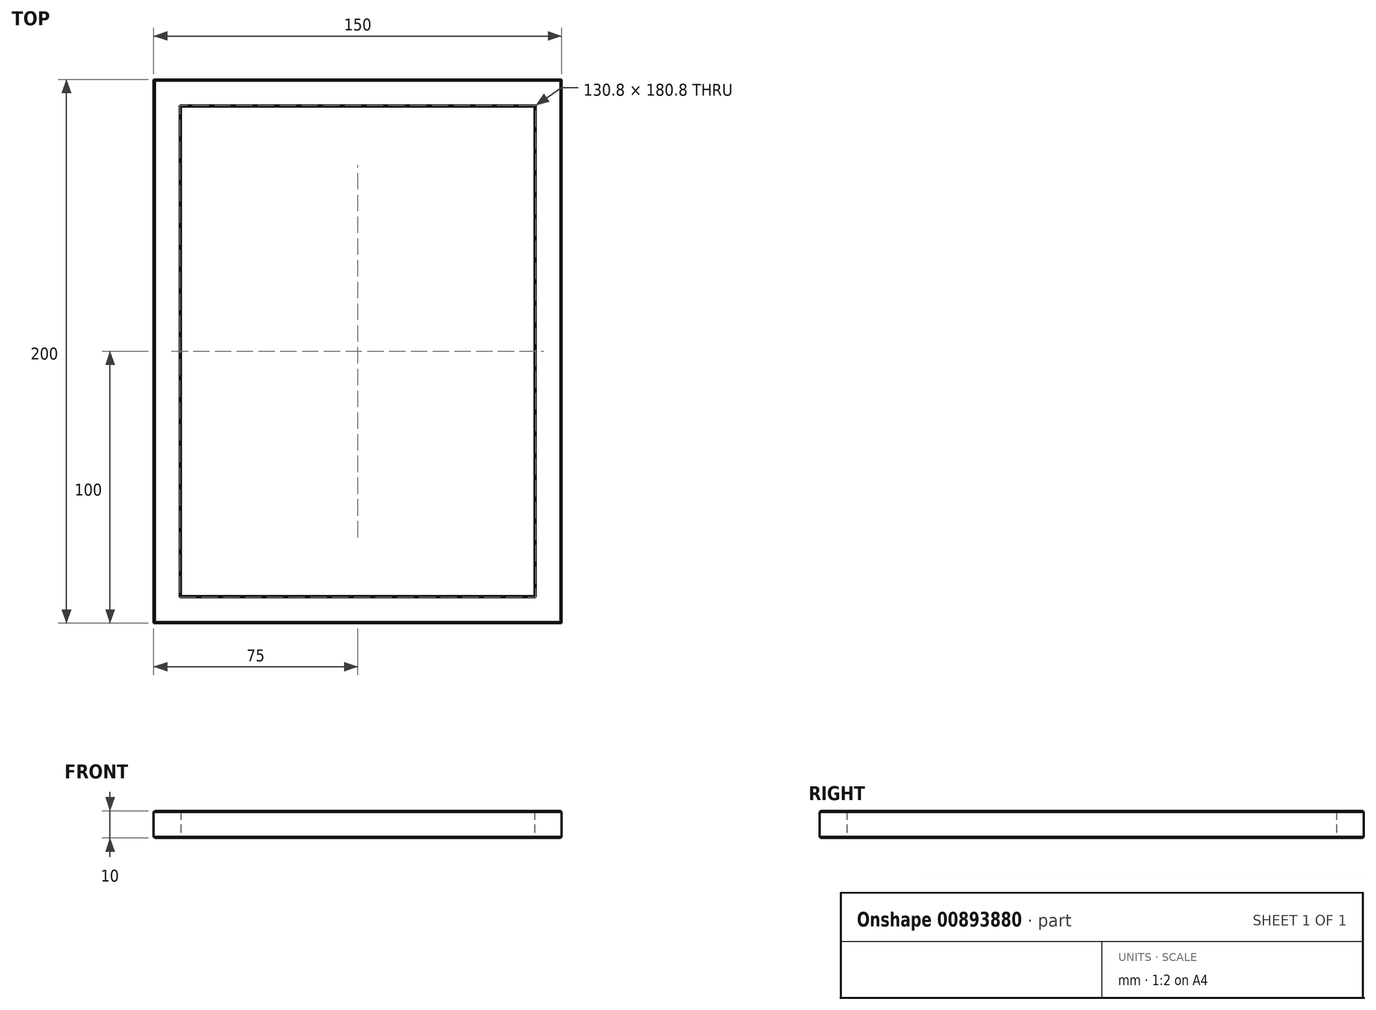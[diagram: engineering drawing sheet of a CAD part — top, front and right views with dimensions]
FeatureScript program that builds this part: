
annotation { "Feature Type Name" : "Feature", "Feature Type Description" : "" }
export const myFeature = defineFeature(function(context is Context, id is Id, definition is map)
    precondition{}
    {
        {
            var Q0;
            Q0=qCreatedBy(makeId("Top.planeOp"),FACE);
            var sketch = newSketch(context, id + "F0", { "sketchPlane" : qUnion([Q0])});
            skLineSegment(sketch, "E0.bottom", {"start": v(75, 100) * mm, "end": v(-75, 100) * mm});
            skLineSegment(sketch, "E0.top", {"start": v(75, -100) * mm, "end": v(-75, -100) * mm});
            skLineSegment(sketch, "E0.left", {"start": v(75, 100) * mm, "end": v(75, -100) * mm});
            skLineSegment(sketch, "E0.right", {"start": v(-75, 100) * mm, "end": v(-75, -100) * mm});
            skPoint(sketch, "E0.middle", {"position": v(0, 0) * mm});
            skLineSegment(sketch, "E1.bottom", {"start": v(65, 90) * mm, "end": v(-65, 90) * mm});
            skLineSegment(sketch, "E1.top", {"start": v(65, -90) * mm, "end": v(-65, -90) * mm});
            skLineSegment(sketch, "E1.left", {"start": v(65, 90) * mm, "end": v(65, -90) * mm});
            skLineSegment(sketch, "E1.right", {"start": v(-65, 90) * mm, "end": v(-65, -90) * mm});
            skSolve(sketch);
        }
        {
            var Q0;
            Q0=makeQuery(id+"F0.imprint","IMPRINT",FACE,{"disambiguationData":[TD([[makeQuery(id+"F0.imprint","IMPRINT",EDGE,{"derivedFrom":sQuery(id+"F0.wireOp",EDGE,"E0.bottom")}),1.0]])]});
            extrude(context, id + "F1", {"entities" : qUnion([Q0]), "depth" : 10 * mm, "offsetDistance" : 25 * mm});
        }
        {
            var Q0;
            Q0=makeQuery(id+"F1.opExtrude","CAP_FACE",FACE,{"disambiguationData":[OSD([sQuery(id+"F0.wireOp",EDGE,"E0.bottom"),sQuery(id+"F0.wireOp",EDGE,"E0.top"),sQuery(id+"F0.wireOp",EDGE,"E0.left"),sQuery(id+"F0.wireOp",EDGE,"E0.right"),sQuery(id+"F0.wireOp",EDGE,"E1.bottom"),sQuery(id+"F0.wireOp",EDGE,"E1.top"),sQuery(id+"F0.wireOp",EDGE,"E1.left"),sQuery(id+"F0.wireOp",EDGE,"E1.right")])],"isStart":false});
            var Q1;
            Q1=makeQuery(id+"F1.opExtrude","CAP_FACE",FACE,{"disambiguationData":[OSD([sQuery(id+"F0.wireOp",EDGE,"E0.bottom"),sQuery(id+"F0.wireOp",EDGE,"E0.top"),sQuery(id+"F0.wireOp",EDGE,"E0.left"),sQuery(id+"F0.wireOp",EDGE,"E0.right"),sQuery(id+"F0.wireOp",EDGE,"E1.bottom"),sQuery(id+"F0.wireOp",EDGE,"E1.top"),sQuery(id+"F0.wireOp",EDGE,"E1.left"),sQuery(id+"F0.wireOp",EDGE,"E1.right")])],"isStart":true});
            chamfer(context, id + "F2", {"entities" : qUnion([Q0, Q1]), "width" : 0.4 * mm, "tangentPropagation" : true});
        }
    });
